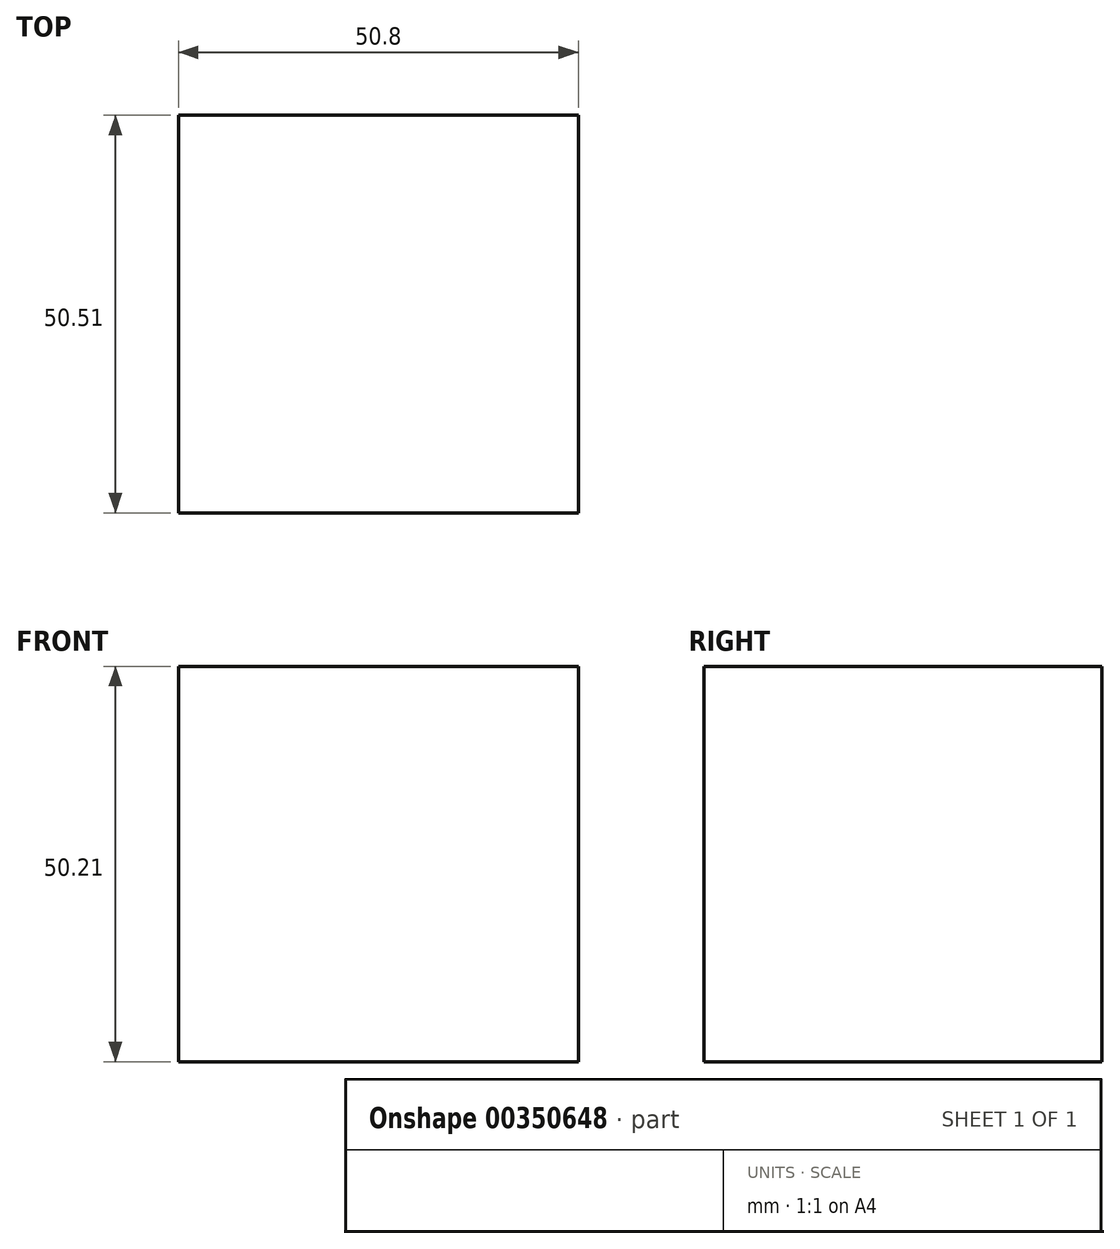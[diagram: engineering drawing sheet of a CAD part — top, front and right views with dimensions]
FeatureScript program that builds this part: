
annotation { "Feature Type Name" : "Feature", "Feature Type Description" : "" }
export const myFeature = defineFeature(function(context is Context, id is Id, definition is map)
    precondition{}
    {
        {
            var Q0;
            Q0=qCreatedBy(makeId("Right.planeOp"),FACE);
            var sketch = newSketch(context, id + "F0", { "sketchPlane" : qUnion([Q0])});
            skLineSegment(sketch, "E0.bottom", {"start": v(-25.86, 36.45) * mm, "end": v(24.65, 36.45) * mm});
            skLineSegment(sketch, "E0.top", {"start": v(-25.86, -13.76) * mm, "end": v(24.65, -13.76) * mm});
            skLineSegment(sketch, "E0.left", {"start": v(-25.86, 36.45) * mm, "end": v(-25.86, -13.76) * mm});
            skLineSegment(sketch, "E0.right", {"start": v(24.65, 36.45) * mm, "end": v(24.65, -13.76) * mm});
            skSolve(sketch);
        }
        {
            var Q0;
            Q0 = qSketchRegion(id + "F0", true);
            extrude(context, id + "F1", {"entities" : qUnion([Q0]), "depth" : 50.8 * mm});
        }
    });
